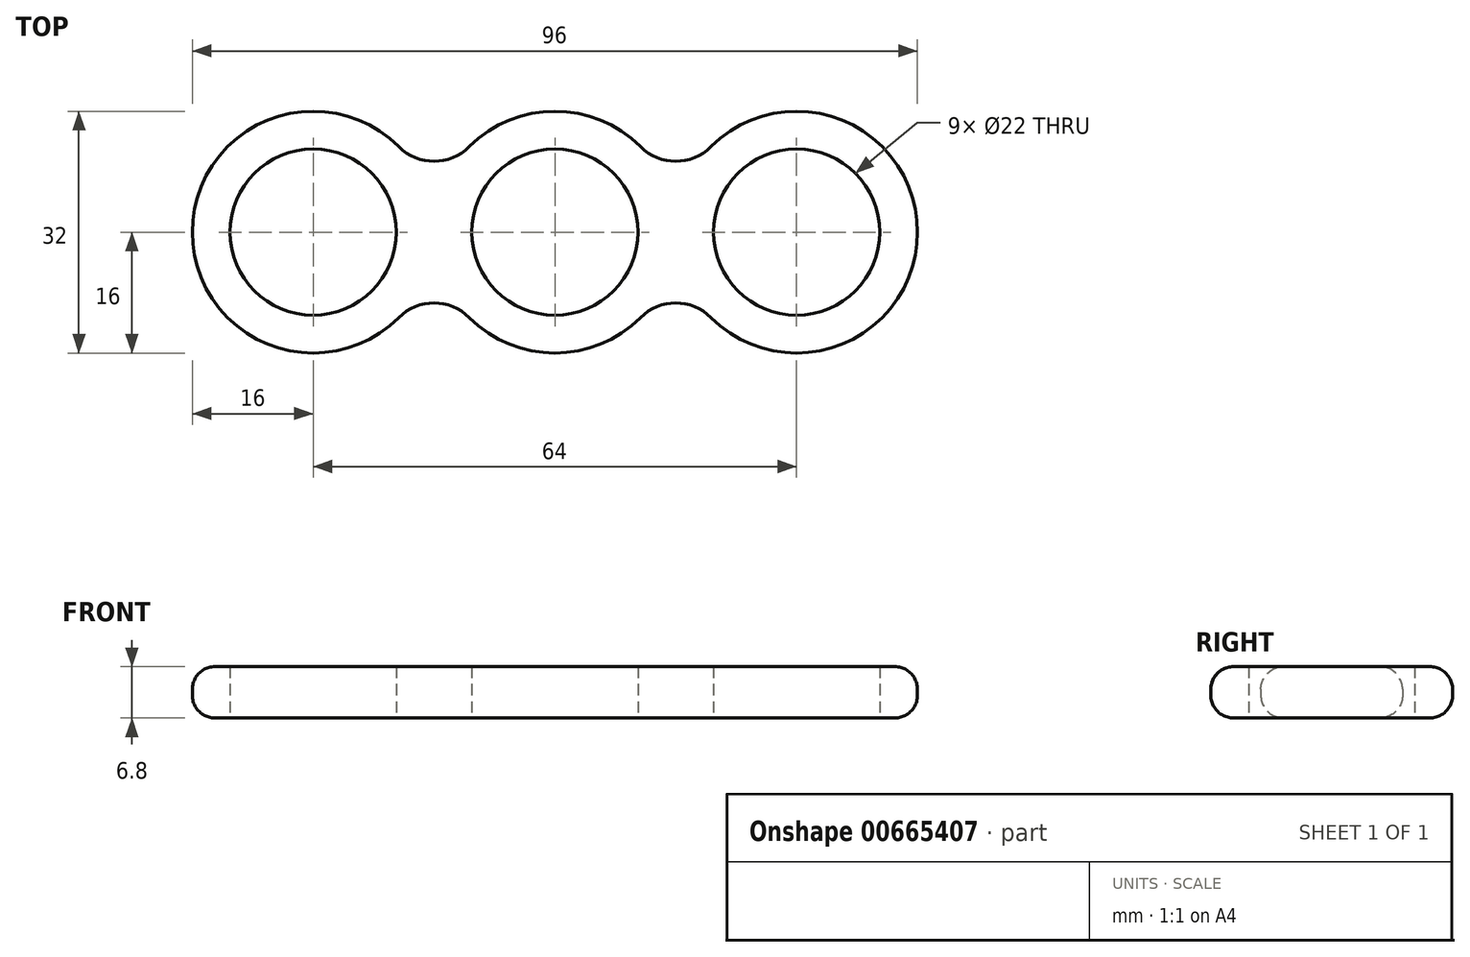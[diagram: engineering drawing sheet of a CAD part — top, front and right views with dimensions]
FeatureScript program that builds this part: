
annotation { "Feature Type Name" : "Feature", "Feature Type Description" : "" }
export const myFeature = defineFeature(function(context is Context, id is Id, definition is map)
    precondition{}
    {
        {
            var Q0;
            Q0=qCreatedBy(makeId("Top.planeOp"),FACE);
            var sketch = newSketch(context, id + "F0", { "sketchPlane" : qUnion([Q0])});
            skLineSegment(sketch, "E0.bottom", {"start": v(48, -16) * mm, "end": v(-48, -16) * mm});
            skLineSegment(sketch, "E0.top", {"start": v(48, 16) * mm, "end": v(-48, 16) * mm});
            skLineSegment(sketch, "E0.left", {"start": v(48, -16) * mm, "end": v(48, 16) * mm});
            skLineSegment(sketch, "E0.right", {"start": v(-48, -16) * mm, "end": v(-48, 16) * mm});
            skPoint(sketch, "E0.middle", {"position": v(0, 0) * mm});
            skLineSegment(sketch, "E1", {"start": v(0, 0) * mm, "end": v(-32, 0) * mm, "construction": true});
            skLineSegment(sketch, "E2", {"start": v(0, 0) * mm, "end": v(32, 0) * mm, "construction": true});
            skCircle(sketch, "E3", {"center": v(-32, 0) * mm, "radius": 11 * mm});
            skCircle(sketch, "E4", {"center": v(0, 0) * mm, "radius": 11 * mm});
            skCircle(sketch, "E5", {"center": v(32, 0) * mm, "radius": 11 * mm});
            skCircle(sketch, "E6", {"center": v(-32, 0) * mm, "radius": 16 * mm});
            skCircle(sketch, "E7", {"center": v(32, 0) * mm, "radius": 16 * mm});
            skCircle(sketch, "E8", {"center": v(0, 0) * mm, "radius": 16 * mm});
            skLineSegment(sketch, "E9.bottom", {"start": v(16, -16) * mm, "end": v(-16, -16) * mm, "construction": true});
            skLineSegment(sketch, "E9.top", {"start": v(16, 16) * mm, "end": v(-16, 16) * mm, "construction": true});
            skLineSegment(sketch, "E9.left", {"start": v(16, -16) * mm, "end": v(16, 16) * mm, "construction": true});
            skLineSegment(sketch, "E9.right", {"start": v(-16, -16) * mm, "end": v(-16, 16) * mm, "construction": true});
            skCircle(sketch, "E10", {"center": v(-16, 16) * mm, "radius": 6.63 * mm});
            skCircle(sketch, "E11", {"center": v(-16, -16) * mm, "radius": 6.63 * mm});
            skCircle(sketch, "E12", {"center": v(16, -16) * mm, "radius": 6.63 * mm});
            skCircle(sketch, "E13", {"center": v(16, 16) * mm, "radius": 6.63 * mm});
            skSolve(sketch);
        }
        {
            var Q0;
            Q0=makeQuery(id+"F0.imprint","IMPRINT",FACE,{"disambiguationData":[TD([[makeQuery(id+"F0.imprint","IMPRINT",EDGE,{"derivedFrom":sQuery(id+"F0.wireOp",EDGE,"E3")}),-1.0]])]});
            var Q1;
            Q1=makeQuery(id+"F0.imprint","IMPRINT",FACE,{"disambiguationData":[TD([[makeQuery(id+"F0.imprint","IMPRINT",EDGE,{"derivedFrom":sQuery(id+"F0.wireOp",EDGE,"E4")}),-1.0]])]});
            var Q2;
            Q2=makeQuery(id+"F0.imprint","IMPRINT",FACE,{"disambiguationData":[TD([[makeQuery(id+"F0.imprint","IMPRINT",EDGE,{"derivedFrom":sQuery(id+"F0.wireOp",EDGE,"E5")}),-1.0]])]});
            var Q3;
            {var subQ0=sQuery(id+"F0.wireOp",EDGE,"E13");var subQ1=sQuery(id+"F0.wireOp",EDGE,"E7");var subQ2=makeQuery(id+"F0.imprint","INTERSECT",VERTEX,{"derivedFrom":[subQ1,subQ0]});Q3=makeQuery(id+"F0.imprint","IMPRINT",FACE,{"disambiguationData":[TD([[makeQuery(id+"F0.imprint","IMPRINT",EDGE,{"disambiguationData":[TD([[subQ2,-1.0]])],"derivedFrom":subQ1}),-1.0]])]});}
            var Q4;
            {var subQ0=sQuery(id+"F0.wireOp",EDGE,"E10");var subQ1=sQuery(id+"F0.wireOp",EDGE,"E6");var subQ2=makeQuery(id+"F0.imprint","INTERSECT",VERTEX,{"derivedFrom":[subQ1,subQ0]});Q4=makeQuery(id+"F0.imprint","IMPRINT",FACE,{"disambiguationData":[TD([[makeQuery(id+"F0.imprint","IMPRINT",EDGE,{"disambiguationData":[TD([[subQ2,1.0]])],"derivedFrom":subQ1}),-1.0]])]});}
            var Q5;
            {var subQ0=sQuery(id+"F0.wireOp",EDGE,"E8");var subQ1=sQuery(id+"F0.wireOp",EDGE,"E6");var subQ2=makeQuery(id+"F0.imprint","INTERSECT",VERTEX,{"derivedFrom":[subQ1,subQ0]});Q5=makeQuery(id+"F0.imprint","IMPRINT",FACE,{"disambiguationData":[TD([[makeQuery(id+"F0.imprint","IMPRINT",EDGE,{"disambiguationData":[TD([[subQ2,1.0]])],"derivedFrom":subQ1}),-1.0]])]});}
            var Q6;
            {var subQ0=sQuery(id+"F0.wireOp",EDGE,"E8");var subQ1=sQuery(id+"F0.wireOp",EDGE,"E7");var subQ2=makeQuery(id+"F0.imprint","INTERSECT",VERTEX,{"derivedFrom":[subQ1,subQ0]});Q6=makeQuery(id+"F0.imprint","IMPRINT",FACE,{"disambiguationData":[TD([[makeQuery(id+"F0.imprint","IMPRINT",EDGE,{"disambiguationData":[TD([[subQ2,-1.0]])],"derivedFrom":subQ1}),-1.0]])]});}
            extrude(context, id + "F1", {"entities" : qUnion([Q0, Q1, Q2, Q3, Q4, Q5, Q6]), "depth" : 6.8 * mm, "offsetDistance" : 25 * mm});
        }
        {
            var Q0;
            Q0=makeQuery(id+"F1.opExtrude","CAP_EDGE",EDGE,{"disambiguationData":[OSD([sQuery(id+"F0.wireOp",EDGE,"E6")])],"isStart":false});
            var Q1;
            Q1=makeQuery(id+"F1.opExtrude","CAP_EDGE",EDGE,{"disambiguationData":[OSD([sQuery(id+"F0.wireOp",EDGE,"E11")])],"isStart":false});
            var Q2;
            {var subQ0=sQuery(id+"F0.wireOp",EDGE,"E8");var subQ1=makeQuery(id+"F0.imprint","INTERSECT",VERTEX,{"derivedFrom":[sQuery(id+"F0.wireOp",EDGE,"E0.bottom"),subQ0]});Q2=makeQuery(id+"F1.opExtrude","CAP_EDGE",EDGE,{"disambiguationData":[OSD([subQ0]),TDD([makeQuery(id+"F0.imprint","IMPRINT",EDGE,{"disambiguationData":[TD([[subQ1,1.0]])],"derivedFrom":subQ0}),makeQuery(id+"F0.imprint","IMPRINT",EDGE,{"disambiguationData":[TD([[subQ1,-1.0]])],"derivedFrom":subQ0})])],"isStart":false});}
            var Q3;
            Q3=makeQuery(id+"F1.opExtrude","CAP_EDGE",EDGE,{"disambiguationData":[OSD([sQuery(id+"F0.wireOp",EDGE,"E12")])],"isStart":false});
            var Q4;
            Q4=makeQuery(id+"F1.opExtrude","CAP_EDGE",EDGE,{"disambiguationData":[OSD([sQuery(id+"F0.wireOp",EDGE,"E7")])],"isStart":false});
            var Q5;
            Q5=makeQuery(id+"F1.opExtrude","CAP_EDGE",EDGE,{"disambiguationData":[OSD([sQuery(id+"F0.wireOp",EDGE,"E10")])],"isStart":false});
            var Q6;
            {var subQ0=sQuery(id+"F0.wireOp",EDGE,"E8");var subQ1=makeQuery(id+"F0.imprint","INTERSECT",VERTEX,{"derivedFrom":[sQuery(id+"F0.wireOp",EDGE,"E0.top"),subQ0]});Q6=makeQuery(id+"F1.opExtrude","CAP_EDGE",EDGE,{"disambiguationData":[OSD([subQ0]),TDD([makeQuery(id+"F0.imprint","IMPRINT",EDGE,{"disambiguationData":[TD([[subQ1,1.0]])],"derivedFrom":subQ0}),makeQuery(id+"F0.imprint","IMPRINT",EDGE,{"disambiguationData":[TD([[subQ1,-1.0]])],"derivedFrom":subQ0})])],"isStart":false});}
            var Q7;
            Q7=makeQuery(id+"F1.opExtrude","CAP_EDGE",EDGE,{"disambiguationData":[OSD([sQuery(id+"F0.wireOp",EDGE,"E13")])],"isStart":false});
            var Q8;
            Q8=makeQuery(id+"F1.opExtrude","CAP_EDGE",EDGE,{"disambiguationData":[OSD([sQuery(id+"F0.wireOp",EDGE,"E6")])],"isStart":true});
            var Q9;
            Q9=makeQuery(id+"F1.opExtrude","CAP_EDGE",EDGE,{"disambiguationData":[OSD([sQuery(id+"F0.wireOp",EDGE,"E11")])],"isStart":true});
            var Q10;
            {var subQ0=sQuery(id+"F0.wireOp",EDGE,"E8");var subQ1=makeQuery(id+"F0.imprint","INTERSECT",VERTEX,{"derivedFrom":[sQuery(id+"F0.wireOp",EDGE,"E0.bottom"),subQ0]});Q10=makeQuery(id+"F1.opExtrude","CAP_EDGE",EDGE,{"disambiguationData":[OSD([subQ0]),TDD([makeQuery(id+"F0.imprint","IMPRINT",EDGE,{"disambiguationData":[TD([[subQ1,1.0]])],"derivedFrom":subQ0}),makeQuery(id+"F0.imprint","IMPRINT",EDGE,{"disambiguationData":[TD([[subQ1,-1.0]])],"derivedFrom":subQ0})])],"isStart":true});}
            var Q11;
            Q11=makeQuery(id+"F1.opExtrude","CAP_EDGE",EDGE,{"disambiguationData":[OSD([sQuery(id+"F0.wireOp",EDGE,"E12")])],"isStart":true});
            var Q12;
            Q12=makeQuery(id+"F1.opExtrude","CAP_EDGE",EDGE,{"disambiguationData":[OSD([sQuery(id+"F0.wireOp",EDGE,"E7")])],"isStart":true});
            var Q13;
            Q13=makeQuery(id+"F1.opExtrude","CAP_EDGE",EDGE,{"disambiguationData":[OSD([sQuery(id+"F0.wireOp",EDGE,"E10")])],"isStart":true});
            var Q14;
            {var subQ0=sQuery(id+"F0.wireOp",EDGE,"E8");var subQ1=makeQuery(id+"F0.imprint","INTERSECT",VERTEX,{"derivedFrom":[sQuery(id+"F0.wireOp",EDGE,"E0.top"),subQ0]});Q14=makeQuery(id+"F1.opExtrude","CAP_EDGE",EDGE,{"disambiguationData":[OSD([subQ0]),TDD([makeQuery(id+"F0.imprint","IMPRINT",EDGE,{"disambiguationData":[TD([[subQ1,1.0]])],"derivedFrom":subQ0}),makeQuery(id+"F0.imprint","IMPRINT",EDGE,{"disambiguationData":[TD([[subQ1,-1.0]])],"derivedFrom":subQ0})])],"isStart":true});}
            var Q15;
            Q15=makeQuery(id+"F1.opExtrude","CAP_EDGE",EDGE,{"disambiguationData":[OSD([sQuery(id+"F0.wireOp",EDGE,"E13")])],"isStart":true});
            fillet(context, id + "F2", {"entities" : qUnion([Q0, Q1, Q2, Q3, Q4, Q5, Q6, Q7, Q8, Q9, Q10, Q11, Q12, Q13, Q14, Q15]), "radius" : 3 * mm, "tangentPropagation" : true, "allowEdgeOverflow" : false});
        }
    });
